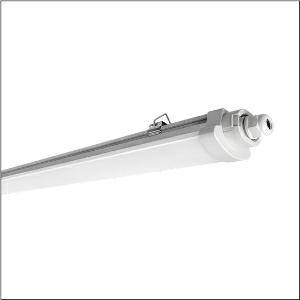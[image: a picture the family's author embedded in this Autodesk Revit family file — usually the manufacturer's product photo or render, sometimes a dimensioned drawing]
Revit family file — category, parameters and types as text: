
# Revit family: monsun_r__41_51fk20mn460a_a5b0
name_source: partatom
category: Lighting Fixtures
units: mm (PartAtom-declared; Revit-internal decimal feet)

## family parameters
Cut with Voids When Loaded = No
Host = Face
Light Source = No
Part Type = Normal
Room Calculation Point = No
Round Connector Dimension = Use Diameter
Shared = No

## types (1)
- --- (1 x LED, 6000 lm, 46 W, 4000K)
    Apparent Load = 46 VA
    CIE Flux Codes = 44 74 91 91 100
    Color Rendering = 80
    Color Temperature = 4000K
    Default Elevation = 1800 mm
    Description = Monsun® 41, damp-proof luminaire, primary optical cover: diffuser, of PC, frosted, light emission: direct distribution, primary light characteristic: symmetric, installation type: suspended mounting, surface-mounted, LED, rated luminous flux: 6.000lm, luminous efficacy: 130lm/W, light colour: 840, colour temperature: 4000K, control gear: ECG Multilumen, with terminal, 3-pole, mains connection: 220..240V, AC, 50/60Hz, rated input power: 46W, housing, luminaire housing, of PC, grey, length: 1.500mm, width: 79mm, height: 52mm, end cap, of PC, grey, ceiling mounting element, of stainless steel (V2A), protection rating (complete): IP65, insulation class (complete): insulation class II (safety insulation), certification: CE, UKCA, protection symbol: D, impact resistance: IK08, permissible operating ambient temperature: -20..+35°C, corresponds to IFS (International Featured Standards) requirements for safety and quality in the food industry, contact your sales advisor before using the luminaires in applications with unclear chemical exposure, large temperature fluctuations or condensation-forming humidity, packaging unit: 1 piece
    Height = 54 mm
    Lamp = 1 x LED
    Lamp Light Flux = 6000 lm
    Lamp Power = 46 W
    Lamp count = 1
    Length = 1500 mm
    Luminous efficacy = 130 lm/W
    Manufacturer = Siteco
    ModVariant = No
    Model = 51FK20MN460A
    Mounting Place = Ceiling
    Mounting Type = Surface mounted
    Number of Poles = 1
    OnlyDefault = Yes
    Power Factor = 1
    Product Name = Monsun® 41
    Product group = damp-proof luminaire
    ProductGroupID = 300
    Protection Class = Protection class II
    Protection Degree = IP 65
    RLX_Detail_Level = 1
    RLX_Emergency_Light_Flux = 0 lm
    RLX_Emergency_Type = 0
    RLX_Emergency_Type_DB = No
    RlxData = <blob elided: 28901 chars, md5=9fac2033>
    Socket = socket
    Standby Power = 0 W
    System Light Flux = 6000 lm
    System Power = 46 W
    Type Comments = factory setting: luminous flux: 100 % | (HIGH)
    Type Image = l_1007037.jpg
    URL = http://relux.com
    VarID = @adj_107849
    Voltage = 0 V
    Weight = 0.00 kg
    Width = 79 mm

## geometry (parser evidence)
native form markers: Blend x4, Sweep x12
no freeform markers — native parametric forms only
